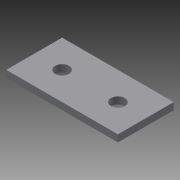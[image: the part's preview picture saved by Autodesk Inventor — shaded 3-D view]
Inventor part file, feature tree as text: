
AUTODESK INVENTOR PART (.ipt)
format: ipt  version: 2015 SP1 (Build 190203100, 203)  size: 81,408 bytes
history: native  units: in
note: dims shown in document units (in); Inventor stores cm internally (conversion verified against a paired STEP export)
features: sketch x2, extrude x1, hole x1
ambient origin geometry x8: Origin, YZ Plane, XZ Plane, XY Plane, X Axis, Y Axis, Z Axis, Center Point
bodies: Solid1 (feature_tree)
feature tree (4):
  extrude  "Extrusion1"  Depth=1.0in
  hole  "Hole1"  [1 undecoded]
  sketch  "Sketch1"  dims[d0=3.0in d1=1.0in]
  sketch  "Sketch2"  dims[d2=0.125in d3=0.0in d4=0.5in d5=0.5in d6=0.5in d7=0.5in d8=0.25in d9=0.75in d10=0.375in d11=0.25in d12=0.5635in d13=1.0in d14=0.8108in]
note: 1 required parameter value undecoded (feature->parameter linkage not recoverable at this tier; creation-order binding heuristic only, values carry confidence <= 0.55)
